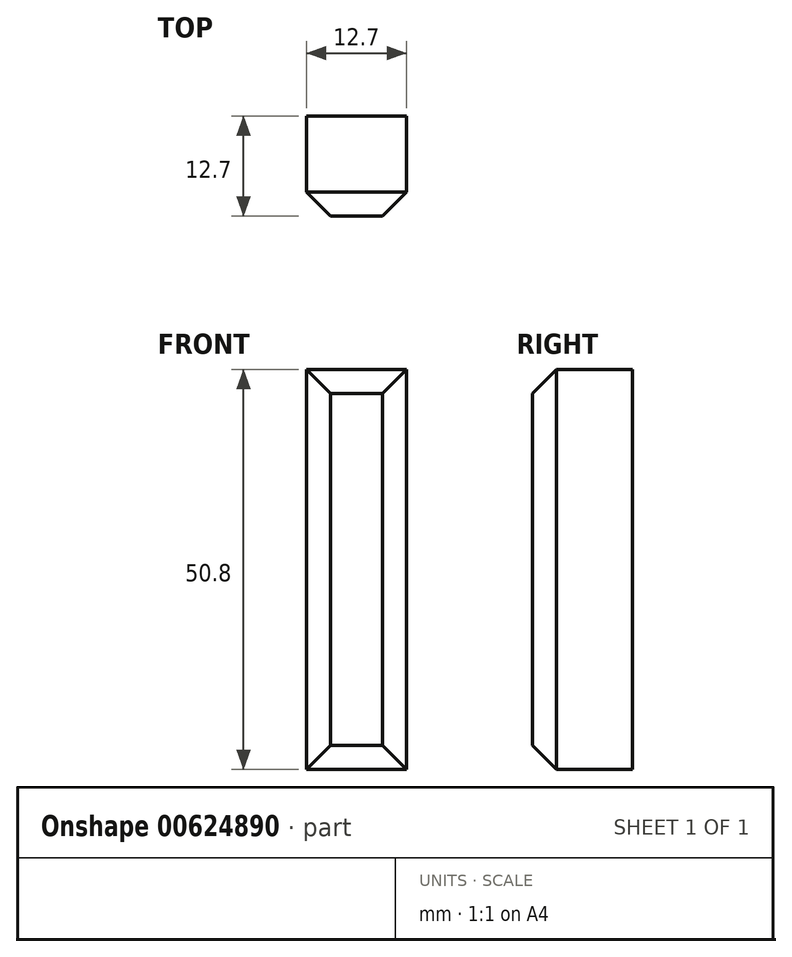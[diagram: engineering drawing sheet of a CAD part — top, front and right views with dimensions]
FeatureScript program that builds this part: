
annotation { "Feature Type Name" : "Feature", "Feature Type Description" : "" }
export const myFeature = defineFeature(function(context is Context, id is Id, definition is map)
    precondition{}
    {
        {
            var Q0;
            Q0=qCreatedBy(makeId("Front.planeOp"),FACE);
            var sketch = newSketch(context, id + "F0", { "sketchPlane" : qUnion([Q0])});
            skLineSegment(sketch, "E0.bottom", {"start": v(0, 0) * mm, "end": v(-12.7, 0) * mm});
            skLineSegment(sketch, "E0.top", {"start": v(0, 50.8) * mm, "end": v(-12.7, 50.8) * mm});
            skLineSegment(sketch, "E0.left", {"start": v(0, 0) * mm, "end": v(0, 50.8) * mm});
            skLineSegment(sketch, "E0.right", {"start": v(-12.7, 0) * mm, "end": v(-12.7, 50.8) * mm});
            skSolve(sketch);
        }
        {
            var Q0;
            Q0=makeQuery(id+"F0.imprint","IMPRINT",FACE,{"disambiguationData":[TD([[makeQuery(id+"F0.imprint","IMPRINT",EDGE,{"derivedFrom":sQuery(id+"F0.wireOp",EDGE,"E0.bottom")}),-1.0]])]});
            extrude(context, id + "F1", {"entities" : qUnion([Q0]), "depth" : 12.7 * mm, "offsetDistance" : 25.4 * mm});
        }
        {
            var Q0;
            Q0=makeQuery(id+"F1.opExtrude","CAP_EDGE",EDGE,{"disambiguationData":[OSD([sQuery(id+"F0.wireOp",EDGE,"E0.right")])],"isStart":false});
            var Q1;
            Q1=makeQuery(id+"F1.opExtrude","CAP_EDGE",EDGE,{"disambiguationData":[OSD([sQuery(id+"F0.wireOp",EDGE,"E0.bottom")])],"isStart":false});
            var Q2;
            Q2=makeQuery(id+"F1.opExtrude","CAP_EDGE",EDGE,{"disambiguationData":[OSD([sQuery(id+"F0.wireOp",EDGE,"E0.left")])],"isStart":false});
            var Q3;
            Q3=makeQuery(id+"F1.opExtrude","CAP_EDGE",EDGE,{"disambiguationData":[OSD([sQuery(id+"F0.wireOp",EDGE,"E0.top")])],"isStart":false});
            chamfer(context, id + "F2", {"entities" : qUnion([Q0, Q1, Q2, Q3]), "width" : 3.05 * mm, "tangentPropagation" : true});
        }
    });
